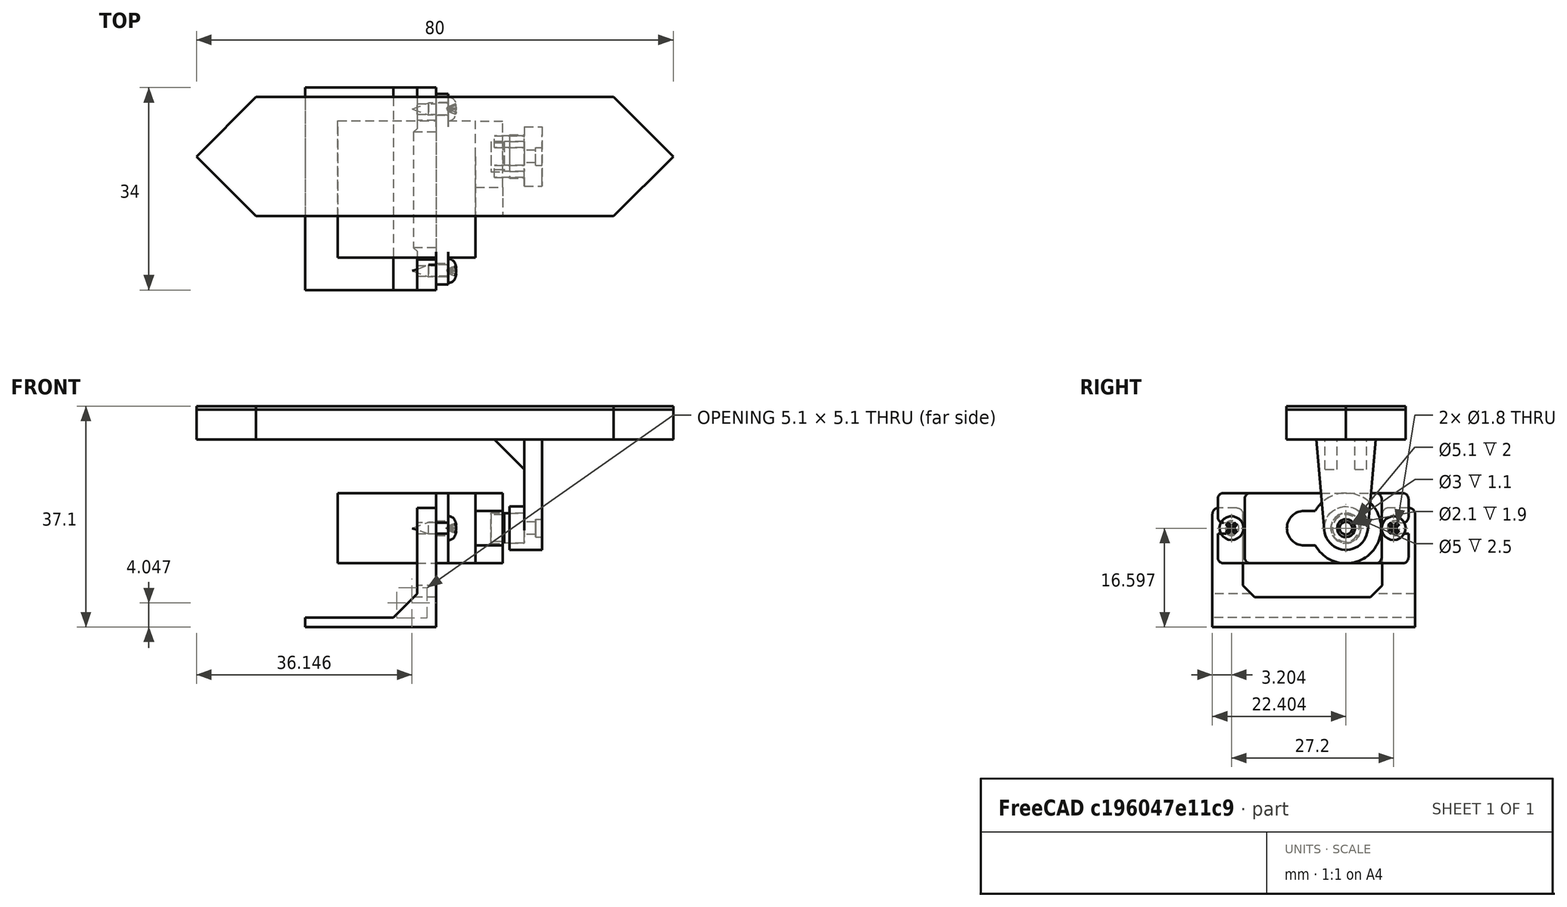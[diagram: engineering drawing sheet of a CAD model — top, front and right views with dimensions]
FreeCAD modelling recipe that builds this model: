
FCSTD DOCUMENT  (FreeCAD 0.20R29603 (Git))
Label: Segment_Assembly
License: All rights reserved
LicenseURL: http://en.wikipedia.org/wiki/All_rights_reserved
objects: App::FeaturePython×26, Part::FeaturePython×7
note: 7 computed .brp shape members not serialized (recipe doc carries the construction recipe); baked Part::Feature solids carry a one-line shape summary decoded from their .brp

FEATURE [Part::FeaturePython] b_SG90_Assembly_001_  label="SG90_Assembly_SG90_Corpo_Body_001_001"  # a2plus imported part (geometry in sourceFile) (typed FeaturePython)
  Placement = pos=(6.00603,24.8242,29.8766) rot=(0.57735,0.57735,0.57735;2.0944rad)
  a2p_Version = 0.4.60i
  fixedPosition = true
  objectType = a2pPart
  sourceFile = ./../SG90/SG90_Assembly.FCStd
  sourcePart = SG90_Corpo_Body_001
  subassemblyImport = true
  timeLastImport = 1.67509e+09
  updateColors = true
FEATURE [Part::FeaturePython] b_SG90_Assembly_001_001  label="SG90_Assembly_SG90_Eixo_Body_001_001"  # a2plus imported part (geometry in sourceFile) (typed FeaturePython)
  Placement = pos=(6.01255,24.8685,29.841) rot=(0.577013,0.578025,0.577013;2.09338rad)
  a2p_Version = 0.4.60i
  fixedPosition = true
  objectType = a2pPart
  sourceFile = ./../SG90/SG90_Assembly.FCStd
  sourcePart = SG90_Eixo_Body_001
  subassemblyImport = true
  timeLastImport = 1.67509e+09
  updateColors = true
FEATURE [Part::FeaturePython] b_Segment_80x20_001_  label="Segment_80x20_Body_001"  # a2plus imported part (geometry in sourceFile) (typed FeaturePython)
  Placement = pos=(22.306,30.3206,49.7766) rot=(1,0,0;3.14178rad)
  a2p_Version = 0.4.60i
  fixedPosition = false
  objectType = a2pPart
  sourceFile = ./Segment_80x20.FCStd
  sourcePart = Body
  subassemblyImport = false
  timeLastImport = 1.67507e+09
  updateColors = true
FEATURE [Part::FeaturePython] b_FacePlate_80x20_001_  label="FacePlate_80x20_Body_001"  # a2plus imported part (geometry in sourceFile) (typed FeaturePython)
  Placement = pos=(22.306,30.3205,50.3766) rot=(0,1,9.2e-05;3.14159rad)
  a2p_Version = 0.4.60i
  fixedPosition = false
  objectType = a2pPart
  sourceFile = ./FacePlate_80x20.FCStd
  sourcePart = Body
  subassemblyImport = false
  timeLastImport = 1.67507e+09
  updateColors = true
FEATURE [App::FeaturePython] axisCoincident_001  label="axisCoincident_001__SG90_Assembly_SG90_Corpo_Body_001_001"  # a2plus constraint (typed FeaturePython)
  Object1 = b_SG90_Assembly_001_001
  Object2 = b_SG90_Assembly_001_
  ParentTreeObject = -> b_SG90_Assembly_001_001
  SubElement1 = Face4
  SubElement2 = Face48
  Suppressed = false
  Type = axial
  directionConstraint = 1
  lockRotation = false
FEATURE [App::FeaturePython] axisCoincident_001_mirror  label="axisCoincident_001__SG90_Assembly_SG90_Eixo_Body_001_001"  # a2plus constraint (typed FeaturePython)
  Object1 = b_SG90_Assembly_001_001
  Object2 = b_SG90_Assembly_001_
  ParentTreeObject = -> b_SG90_Assembly_001_
  SubElement1 = Face4
  SubElement2 = Face48
  Suppressed = false
  Type = axial
  directionConstraint = 1
  lockRotation = false
FEATURE [App::FeaturePython] planeCoincident_001  label="planeCoincident_001__SG90_Assembly_SG90_Eixo_Body_001_001"  # a2plus constraint (typed FeaturePython)
  Object1 = b_SG90_Assembly_001_
  Object2 = b_SG90_Assembly_001_001
  ParentTreeObject = -> b_SG90_Assembly_001_
  SubElement1 = Face49
  SubElement2 = Face5
  Suppressed = false
  Type = plane
  directionConstraint = 0
  offset = 0
FEATURE [App::FeaturePython] planeCoincident_001_mirror  label="planeCoincident_001__SG90_Assembly_SG90_Corpo_Body_001_001"  # a2plus constraint (typed FeaturePython)
  Object1 = b_SG90_Assembly_001_
  Object2 = b_SG90_Assembly_001_001
  ParentTreeObject = -> b_SG90_Assembly_001_001
  SubElement1 = Face49
  SubElement2 = Face5
  Suppressed = false
  Type = plane
  directionConstraint = 0
  offset = 0
FEATURE [App::FeaturePython] planeCoincident_002  label="planeCoincident_002__FacePlate_80x20_Body_001"  # a2plus constraint (typed FeaturePython)
  Object1 = b_Segment_80x20_001_
  Object2 = b_FacePlate_80x20_001_
  ParentTreeObject = -> b_Segment_80x20_001_
  SubElement1 = Face4
  SubElement2 = Face8
  Suppressed = false
  Type = plane
  directionConstraint = 0
  offset = 0
FEATURE [App::FeaturePython] planeCoincident_002_mirror  label="planeCoincident_002__Segment_80x20_Body_001"  # a2plus constraint (typed FeaturePython)
  Object1 = b_Segment_80x20_001_
  Object2 = b_FacePlate_80x20_001_
  ParentTreeObject = -> b_FacePlate_80x20_001_
  SubElement1 = Face4
  SubElement2 = Face8
  Suppressed = false
  Type = plane
  directionConstraint = 0
  offset = 0
FEATURE [App::FeaturePython] planeCoincident_003  label="planeCoincident_003__Segment_80x20_Body_001"  # a2plus constraint (typed FeaturePython)
  Object1 = b_FacePlate_80x20_001_
  Object2 = b_Segment_80x20_001_
  ParentTreeObject = -> b_FacePlate_80x20_001_
  SubElement1 = Face4
  SubElement2 = Face1
  Suppressed = false
  Type = plane
  directionConstraint = 1
  offset = 0
FEATURE [App::FeaturePython] planeCoincident_003_mirror  label="planeCoincident_003__FacePlate_80x20_Body_001"  # a2plus constraint (typed FeaturePython)
  Object1 = b_FacePlate_80x20_001_
  Object2 = b_Segment_80x20_001_
  ParentTreeObject = -> b_Segment_80x20_001_
  SubElement1 = Face4
  SubElement2 = Face1
  Suppressed = false
  Type = plane
  directionConstraint = 1
  offset = 0
FEATURE [App::FeaturePython] planeCoincident_004  label="planeCoincident_004__Segment_80x20_Body_001"  # a2plus constraint (typed FeaturePython)
  Object1 = b_FacePlate_80x20_001_
  Object2 = b_Segment_80x20_001_
  ParentTreeObject = -> b_FacePlate_80x20_001_
  SubElement1 = Face5
  SubElement2 = Face3
  Suppressed = false
  Type = plane
  directionConstraint = 0
  offset = 0
FEATURE [App::FeaturePython] planeCoincident_004_mirror  label="planeCoincident_004__FacePlate_80x20_Body_001"  # a2plus constraint (typed FeaturePython)
  Object1 = b_FacePlate_80x20_001_
  Object2 = b_Segment_80x20_001_
  ParentTreeObject = -> b_Segment_80x20_001_
  SubElement1 = Face5
  SubElement2 = Face3
  Suppressed = false
  Type = plane
  directionConstraint = 0
  offset = 0
FEATURE [App::FeaturePython] axisCoincident_002  label="axisCoincident_002__SG90_Assembly_SG90_Eixo_Body_001_001"  # a2plus constraint (typed FeaturePython)
  Object1 = b_Segment_80x20_001_
  Object2 = b_SG90_Assembly_001_001
  ParentTreeObject = -> b_Segment_80x20_001_
  SubElement1 = Face25
  SubElement2 = Face1
  Suppressed = false
  Type = axial
  directionConstraint = 1
  lockRotation = false
FEATURE [App::FeaturePython] axisCoincident_002_mirror  label="axisCoincident_002__Segment_80x20_Body_001"  # a2plus constraint (typed FeaturePython)
  Object1 = b_Segment_80x20_001_
  Object2 = b_SG90_Assembly_001_001
  ParentTreeObject = -> b_SG90_Assembly_001_001
  SubElement1 = Face25
  SubElement2 = Face1
  Suppressed = false
  Type = axial
  directionConstraint = 1
  lockRotation = false
FEATURE [App::FeaturePython] planeCoincident_005  label="planeCoincident_005__SG90_Assembly_SG90_Eixo_Body_001_001"  # a2plus constraint (typed FeaturePython)
  Object1 = b_Segment_80x20_001_
  Object2 = b_SG90_Assembly_001_001
  ParentTreeObject = -> b_Segment_80x20_001_
  SubElement1 = Face26
  SubElement2 = Face3
  Suppressed = false
  Type = plane
  directionConstraint = 0
  offset = 0
FEATURE [App::FeaturePython] planeCoincident_005_mirror  label="planeCoincident_005__Segment_80x20_Body_001"  # a2plus constraint (typed FeaturePython)
  Object1 = b_Segment_80x20_001_
  Object2 = b_SG90_Assembly_001_001
  ParentTreeObject = -> b_SG90_Assembly_001_001
  SubElement1 = Face26
  SubElement2 = Face3
  Suppressed = false
  Type = plane
  directionConstraint = 0
  offset = 0
FEATURE [Part::FeaturePython] b_Digit_80x20_Bracket_001_  label="Digit_80x20_Bracket_001"  # a2plus imported part (geometry in sourceFile) (typed FeaturePython)
  Placement = pos=(22.506,41.9242,13.2766) rot=(0,0,1;0rad)
  a2p_Version = 0.4.60i
  fixedPosition = false
  objectType = a2pPart
  sourceFile = ./Digit_80x20_Bracket.FCStd
  subassemblyImport = false
  timeLastImport = 1.67516e+09
  updateColors = true
FEATURE [App::FeaturePython] planeCoincident_006  label="planeCoincident_006__Digit_80x20_Bracket_001"  # a2plus constraint (typed FeaturePython)
  Object1 = b_SG90_Assembly_001_
  Object2 = b_Digit_80x20_Bracket_001_
  ParentTreeObject = -> b_SG90_Assembly_001_
  SubElement1 = Face23
  SubElement2 = Face1
  Suppressed = false
  Type = plane
  directionConstraint = 0
  offset = 0
FEATURE [App::FeaturePython] planeCoincident_006_mirror  label="planeCoincident_006__SG90_Assembly_SG90_Corpo_Body_001_001"  # a2plus constraint (typed FeaturePython)
  Object1 = b_SG90_Assembly_001_
  Object2 = b_Digit_80x20_Bracket_001_
  ParentTreeObject = -> b_Digit_80x20_Bracket_001_
  SubElement1 = Face23
  SubElement2 = Face1
  Suppressed = false
  Type = plane
  directionConstraint = 0
  offset = 0
FEATURE [App::FeaturePython] axisCoincident_003  label="axisCoincident_003__SG90_Assembly_SG90_Corpo_Body_001_001"  # a2plus constraint (typed FeaturePython)
  Object1 = b_Digit_80x20_Bracket_001_
  Object2 = b_SG90_Assembly_001_
  ParentTreeObject = -> b_Digit_80x20_Bracket_001_
  SubElement1 = Face16
  SubElement2 = Face38
  Suppressed = false
  Type = axial
  directionConstraint = 0
  lockRotation = false
FEATURE [App::FeaturePython] axisCoincident_003_mirror  label="axisCoincident_003__Digit_80x20_Bracket_001"  # a2plus constraint (typed FeaturePython)
  Object1 = b_Digit_80x20_Bracket_001_
  Object2 = b_SG90_Assembly_001_
  ParentTreeObject = -> b_SG90_Assembly_001_
  SubElement1 = Face16
  SubElement2 = Face38
  Suppressed = false
  Type = axial
  directionConstraint = 0
  lockRotation = false
FEATURE [Part::FeaturePython] Screw  label="2 mmx6-Screw"  # Fasteners workbench fastener (typed FeaturePython)
  Placement = pos=(24.506,11.1242,29.8766) rot=(0,1,0;1.5708rad)
  diameter = 1
  invert = false
  leftHanded = false
  length = 4
  lengthCustom = 6
  matchOuter = false
  offset = 0
  thread = false
  type = 28
FEATURE [App::FeaturePython] axisCoincident_004  label="axisCoincident_004__Digit_80x20_Bracket_001"  # a2plus constraint (typed FeaturePython)
  Object1 = Screw
  Object2 = b_Digit_80x20_Bracket_001_
  ParentTreeObject = -> Screw
  SubElement1 = Face25
  SubElement2 = Face16
  Suppressed = false
  Type = axial
  directionConstraint = 1
  lockRotation = false
FEATURE [App::FeaturePython] axisCoincident_004_mirror  label="axisCoincident_004__2 mmx6-Screw"  # a2plus constraint (typed FeaturePython)
  Object1 = Screw
  Object2 = b_Digit_80x20_Bracket_001_
  ParentTreeObject = -> b_Digit_80x20_Bracket_001_
  SubElement1 = Face25
  SubElement2 = Face16
  Suppressed = false
  Type = axial
  directionConstraint = 1
  lockRotation = false
FEATURE [App::FeaturePython] planeCoincident_007  label="planeCoincident_007__SG90_Assembly_SG90_Corpo_Body_001_001"  # a2plus constraint (typed FeaturePython)
  Object1 = Screw
  Object2 = b_SG90_Assembly_001_
  ParentTreeObject = -> Screw
  SubElement1 = Face22
  SubElement2 = Face21
  Suppressed = false
  Type = plane
  directionConstraint = 0
  offset = 0
FEATURE [App::FeaturePython] planeCoincident_007_mirror  label="planeCoincident_007__2 mmx6-Screw"  # a2plus constraint (typed FeaturePython)
  Object1 = Screw
  Object2 = b_SG90_Assembly_001_
  ParentTreeObject = -> b_SG90_Assembly_001_
  SubElement1 = Face22
  SubElement2 = Face21
  Suppressed = false
  Type = plane
  directionConstraint = 0
  offset = 0
FEATURE [Part::FeaturePython] Screw001  label="2 mmx6-Screw001"  # Fasteners workbench fastener (typed FeaturePython)
  Placement = pos=(24.506,38.3242,29.8766) rot=(0,1,0;1.5708rad)
  diameter = 1
  invert = false
  leftHanded = false
  length = 4
  lengthCustom = 6
  matchOuter = false
  offset = 0
  thread = false
  type = 28
FEATURE [App::FeaturePython] axisCoincident_005  label="axisCoincident_005__Digit_80x20_Bracket_001"  # a2plus constraint (typed FeaturePython)
  Object1 = Screw001
  Object2 = b_Digit_80x20_Bracket_001_
  ParentTreeObject = -> Screw001
  SubElement1 = Face25
  SubElement2 = Face17
  Suppressed = false
  Type = axial
  directionConstraint = 1
  lockRotation = false
FEATURE [App::FeaturePython] axisCoincident_005_mirror  label="axisCoincident_005__2 mmx6-Screw001"  # a2plus constraint (typed FeaturePython)
  Object1 = Screw001
  Object2 = b_Digit_80x20_Bracket_001_
  ParentTreeObject = -> b_Digit_80x20_Bracket_001_
  SubElement1 = Face25
  SubElement2 = Face17
  Suppressed = false
  Type = axial
  directionConstraint = 1
  lockRotation = false
FEATURE [App::FeaturePython] planeCoincident_008  label="planeCoincident_008__2 mmx6-Screw001"  # a2plus constraint (typed FeaturePython)
  Object1 = b_SG90_Assembly_001_
  Object2 = Screw001
  ParentTreeObject = -> b_SG90_Assembly_001_
  SubElement1 = Face1
  SubElement2 = Face22
  Suppressed = false
  Type = plane
  directionConstraint = 0
  offset = 0
FEATURE [App::FeaturePython] planeCoincident_008_mirror  label="planeCoincident_008__SG90_Assembly_SG90_Corpo_Body_001_001"  # a2plus constraint (typed FeaturePython)
  Object1 = b_SG90_Assembly_001_
  Object2 = Screw001
  ParentTreeObject = -> Screw001
  SubElement1 = Face1
  SubElement2 = Face22
  Suppressed = false
  Type = plane
  directionConstraint = 0
  offset = 0
